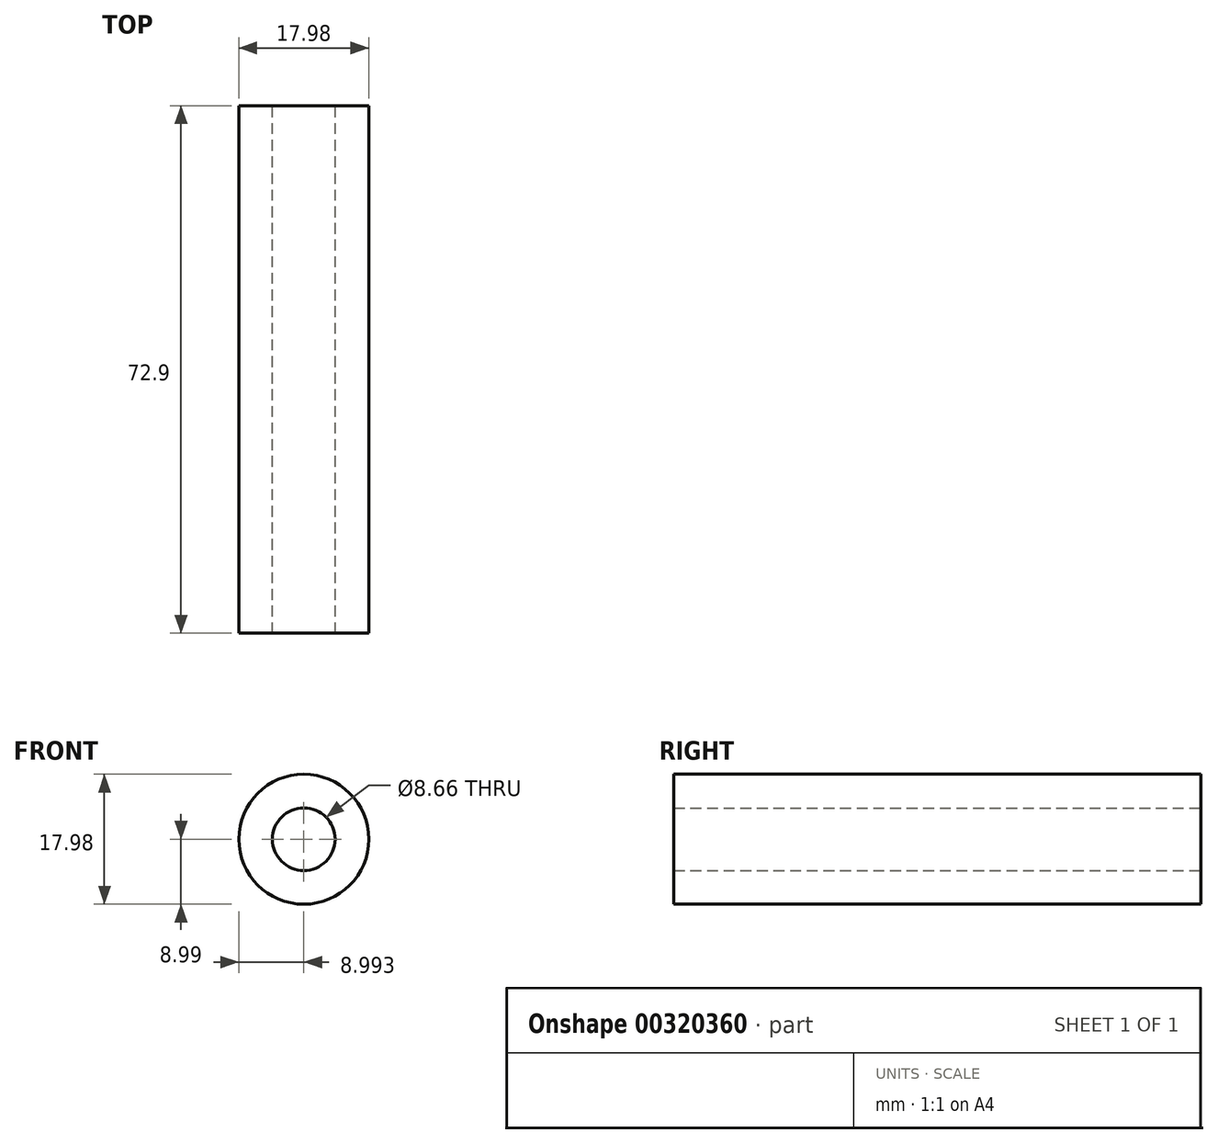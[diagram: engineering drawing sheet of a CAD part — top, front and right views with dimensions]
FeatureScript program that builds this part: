
annotation { "Feature Type Name" : "Feature", "Feature Type Description" : "" }
export const myFeature = defineFeature(function(context is Context, id is Id, definition is map)
    precondition{}
    {
        {
            var Q0;
            Q0=qCreatedBy(makeId("Front.planeOp"),FACE);
            var sketch = newSketch(context, id + "F0", { "sketchPlane" : qUnion([Q0])});
            skCircle(sketch, "E0", {"center": v(-43.99, 0) * mm, "radius": 8.99 * mm});
            skCircle(sketch, "E1", {"center": v(-43.99, 0) * mm, "radius": 4.33 * mm});
            skSolve(sketch);
        }
        {
            var Q0;
            Q0=makeQuery(id+"F0.imprint","IMPRINT",FACE,{"disambiguationData":[TD([[makeQuery(id+"F0.imprint","IMPRINT",EDGE,{"derivedFrom":sQuery(id+"F0.wireOp",EDGE,"E0")}),1.0]])]});
            var Q1;
            Q1=sQuery(id+"F0.wireOp",EDGE,"E0");
            var Q2;
            Q2=sQuery(id+"F0.wireOp",EDGE,"E1");
            extrude(context, id + "F1", {"entities" : qUnion([Q0]), "surfaceEntities" : qUnion([Q1, Q2]), "depth" : 72.9 * mm});
        }
    });
